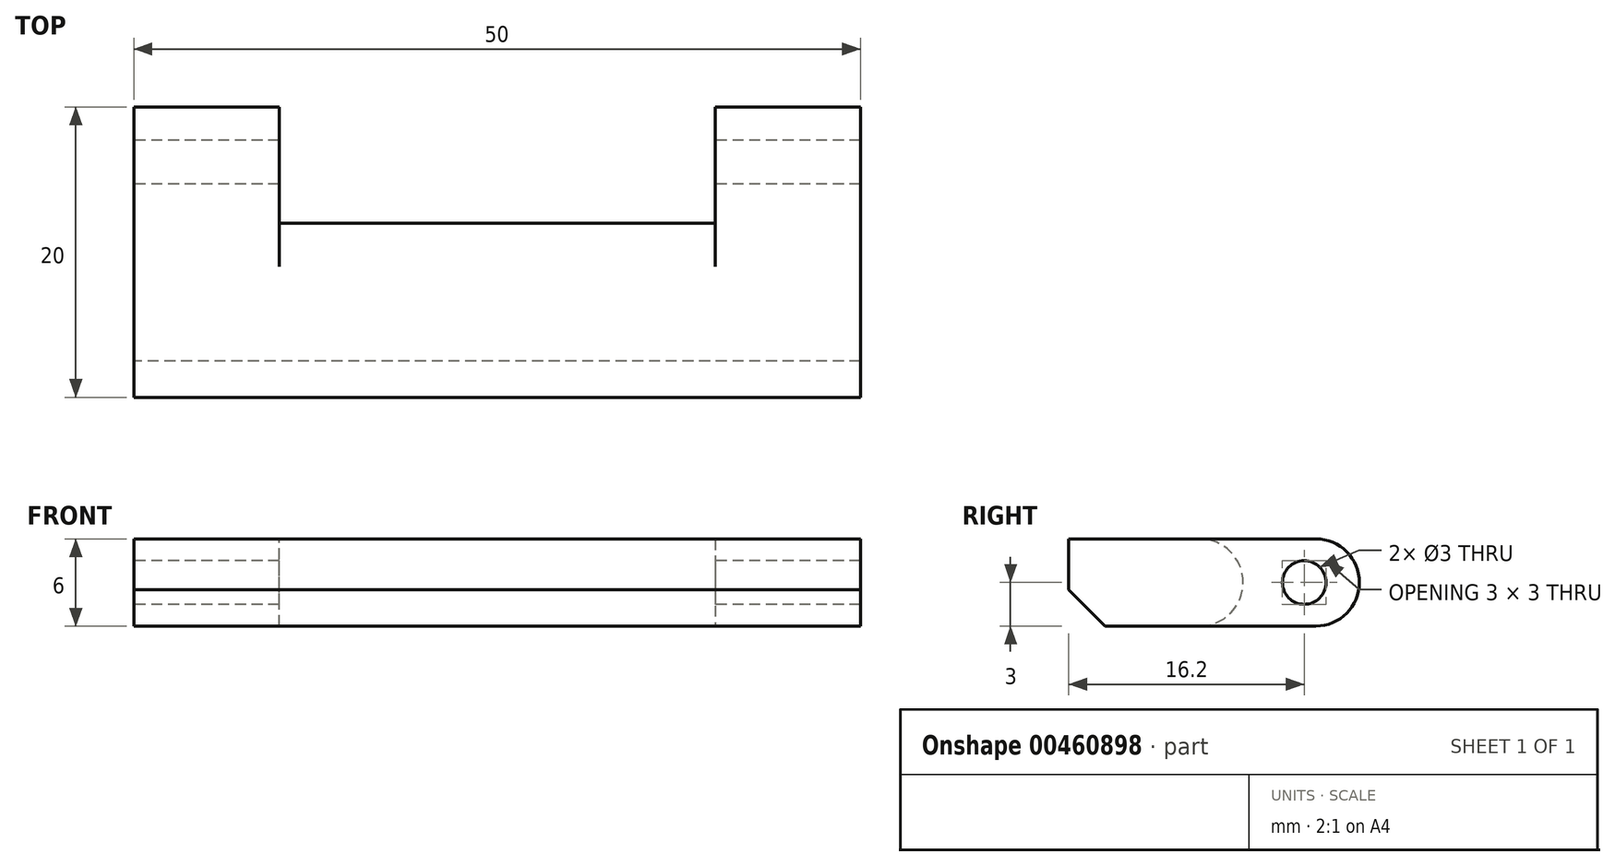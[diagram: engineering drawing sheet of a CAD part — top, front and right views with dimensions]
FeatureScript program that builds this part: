
annotation { "Feature Type Name" : "Feature", "Feature Type Description" : "" }
export const myFeature = defineFeature(function(context is Context, id is Id, definition is map)
    precondition{}
    {
        {
            var Q0;
            Q0=qCreatedBy(makeId("Top.planeOp"),FACE);
            var sketch = newSketch(context, id + "F0", { "sketchPlane" : qUnion([Q0])});
            skLineSegment(sketch, "E0.top", {"start": v(0, -20) * mm, "end": v(50, -20) * mm});
            skLineSegment(sketch, "E0.left", {"start": v(0, 0) * mm, "end": v(0, -20) * mm});
            skLineSegment(sketch, "E0.right", {"start": v(50, 0) * mm, "end": v(50, -20) * mm});
            skLineSegment(sketch, "E1", {"start": v(10, 0) * mm, "end": v(10, -8) * mm});
            skLineSegment(sketch, "E2", {"start": v(10, -8) * mm, "end": v(40, -8) * mm});
            skLineSegment(sketch, "E3", {"start": v(40, -8) * mm, "end": v(40, 0) * mm});
            skLineSegment(sketch, "E4", {"start": v(10, 0) * mm, "end": v(0, 0) * mm});
            skLineSegment(sketch, "E5", {"start": v(40, 0) * mm, "end": v(50, 0) * mm});
            skSolve(sketch);
        }
        {
            var Q0;
            Q0=qSketchRegion(id+"F0",true);
            extrude(context, id + "F1", {"entities" : qUnion([Q0]), "depth" : 6 * mm});
        }
        {
            var Q0;
            Q0=makeQuery(id+"F1.opExtrude","SWEPT_FACE",FACE,{"disambiguationData":[OSD([sQuery(id+"F0.wireOp",EDGE,"E0.left")])]});
            var sketch = newSketch(context, id + "F2", { "sketchPlane" : qUnion([Q0])});
            skCircle(sketch, "E6", {"center": v(3.8, 3) * mm, "radius": 1.5 * mm});
            skSolve(sketch);
        }
        {
            var Q0;
            Q0=makeQuery(id+"F2.imprint","IMPRINT",FACE,{"disambiguationData":[TD([[makeQuery(id+"F2.imprint","IMPRINT",EDGE,{"derivedFrom":sQuery(id+"F2.wireOp",EDGE,"E6")}),1.0]])]});
            extrude(context, id + "F3", {"entities" : qUnion([Q0]), "operationType" : NewBodyOperationType.REMOVE, "endBound" : BoundingType.THROUGH_ALL, "oppositeDirection" : true, "depth" : 25 * mm});
        }
        {
            var Q0;
            Q0=makeQuery(id+"F1.opExtrude","CAP_EDGE",EDGE,{"disambiguationData":[OSD([sQuery(id+"F0.wireOp",EDGE,"E4")])],"isStart":false});
            var Q1;
            Q1=makeQuery(id+"F1.opExtrude","CAP_EDGE",EDGE,{"disambiguationData":[OSD([sQuery(id+"F0.wireOp",EDGE,"E4")])],"isStart":true});
            var Q2;
            Q2=makeQuery(id+"F1.opExtrude","CAP_EDGE",EDGE,{"disambiguationData":[OSD([sQuery(id+"F0.wireOp",EDGE,"E5")])],"isStart":false});
            var Q3;
            Q3=makeQuery(id+"F1.opExtrude","CAP_EDGE",EDGE,{"disambiguationData":[OSD([sQuery(id+"F0.wireOp",EDGE,"E5")])],"isStart":true});
            var Q4;
            Q4=makeQuery(id+"F1.opExtrude","CAP_EDGE",EDGE,{"disambiguationData":[OSD([sQuery(id+"F0.wireOp",EDGE,"E2")])],"isStart":false});
            var Q5;
            Q5=makeQuery(id+"F1.opExtrude","CAP_EDGE",EDGE,{"disambiguationData":[OSD([sQuery(id+"F0.wireOp",EDGE,"E2")])],"isStart":true});
            fillet(context, id + "F4", {"entities" : qUnion([Q0, Q1, Q2, Q3, Q4, Q5]), "radius" : 3 * mm, "tangentPropagation" : true, "allowEdgeOverflow" : false});
        }
        {
            var Q0;
            Q0=makeQuery(id+"F1.opExtrude","CAP_EDGE",EDGE,{"disambiguationData":[OSD([sQuery(id+"F0.wireOp",EDGE,"E0.top")])],"isStart":true});
            chamfer(context, id + "F5", {"entities" : qUnion([Q0]), "width" : 2.5 * mm, "tangentPropagation" : true});
        }
    });
